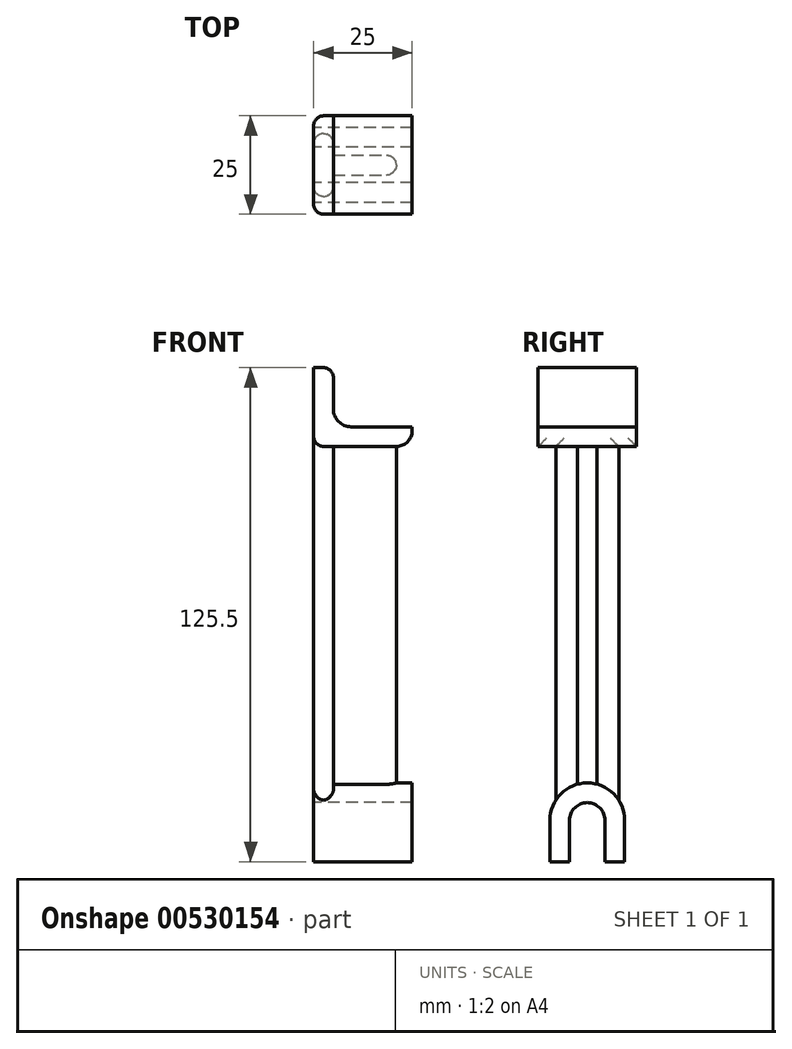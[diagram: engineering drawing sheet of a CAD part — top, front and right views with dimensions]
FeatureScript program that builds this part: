
annotation { "Feature Type Name" : "Feature", "Feature Type Description" : "" }
export const myFeature = defineFeature(function(context is Context, id is Id, definition is map)
    precondition{}
    {
        {
            var Q0;
            Q0=qCreatedBy(makeId("Front.planeOp"),FACE);
            var sketch = newSketch(context, id + "F0", { "sketchPlane" : qUnion([Q0])});
            skCircle(sketch, "E0", {"center": v(0, 104.5) * mm, "radius": 4.5 * mm});
            skLineSegment(sketch, "E1", {"start": v(0, 100) * mm, "end": v(15.5, 100) * mm});
            skLineSegment(sketch, "E2", {"start": v(-4.5, 104.5) * mm, "end": v(-4.5, 115) * mm});
            skLineSegment(sketch, "E3", {"start": v(-4.5, 115) * mm, "end": v(-9.5, 115) * mm});
            skLineSegment(sketch, "E4", {"start": v(-9.5, 115) * mm, "end": v(-9.5, 95) * mm});
            skLineSegment(sketch, "E5", {"start": v(-9.5, 95) * mm, "end": v(15.5, 95) * mm});
            skLineSegment(sketch, "E6", {"start": v(15.5, 95) * mm, "end": v(15.5, 100) * mm});
            skSolve(sketch);
        }
        {
            var Q0;
            {var subQ1=sQuery(id+"F0.wireOp",EDGE,"E1");Q0=makeQuery(id+"F0.imprint","IMPRINT",FACE,{"disambiguationData":[TD([[makeQuery(id+"F0.imprint","IMPRINT",EDGE,{"derivedFrom":subQ1}),-1.0]])]});}
            extrude(context, id + "F1", {"entities" : qUnion([Q0]), "depth" : 25 * mm, "offsetDistance" : 25 * mm, "symmetric" : true});
        }
        {
            var Q0;
            Q0=makeQuery(id+"F1.opExtrude","SWEPT_FACE",FACE,{"disambiguationData":[OSD([sQuery(id+"F0.wireOp",EDGE,"E4")])]});
            var sketch = newSketch(context, id + "F2", { "sketchPlane" : qUnion([Q0])});
            skCircle(sketch, "E7", {"center": v(0, 0) * mm, "radius": 4.5 * mm});
            skLineSegment(sketch, "E8", {"start": v(4.5, 0) * mm, "end": v(4.5, -10.5) * mm});
            skLineSegment(sketch, "E9", {"start": v(4.5, -10.5) * mm, "end": v(9.5, -10.5) * mm});
            skLineSegment(sketch, "E10", {"start": v(9.5, -10.5) * mm, "end": v(9.5, 9.5) * mm});
            skLineSegment(sketch, "E11", {"start": v(9.5, 9.5) * mm, "end": v(-9.5, 9.5) * mm});
            skLineSegment(sketch, "E12", {"start": v(-9.5, 9.5) * mm, "end": v(-9.5, -10.5) * mm});
            skLineSegment(sketch, "E13", {"start": v(-9.5, -10.5) * mm, "end": v(-4.5, -10.5) * mm});
            skLineSegment(sketch, "E14", {"start": v(-4.5, -10.5) * mm, "end": v(-4.5, 0) * mm});
            skArc(sketch, "E15", {"start": v(9.5, 0) * mm, "mid": v(0, 9.5) * mm, "end": v(-9.5, 0) * mm});
            skSolve(sketch);
        }
        {
            var Q0;
            {var subQ4=sQuery(id+"F2.wireOp",EDGE,"E8");Q0=makeQuery(id+"F2.imprint","IMPRINT",FACE,{"disambiguationData":[TD([[makeQuery(id+"F2.imprint","IMPRINT",EDGE,{"derivedFrom":subQ4}),1.0]])]});}
            extrude(context, id + "F3", {"entities" : qUnion([Q0]), "oppositeDirection" : true, "depth" : 25 * mm, "offsetDistance" : 25 * mm});
        }
        {
            var Q0;
            Q0=makeQuery(id+"F1.opExtrude","SWEPT_FACE",FACE,{"disambiguationData":[OSD([sQuery(id+"F0.wireOp",EDGE,"E5")])]});
            var sketch = newSketch(context, id + "F4", { "sketchPlane" : qUnion([Q0])});
            skLineSegment(sketch, "E16.bottom", {"start": v(-9.5, 8) * mm, "end": v(-4.5, 8) * mm});
            skLineSegment(sketch, "E16.top", {"start": v(-9.5, -8) * mm, "end": v(-4.5, -8) * mm});
            skLineSegment(sketch, "E16.left", {"start": v(-9.5, 8) * mm, "end": v(-9.5, -8) * mm});
            skLineSegment(sketch, "E16.right", {"start": v(-4.5, 8) * mm, "end": v(-4.5, -8) * mm});
            skLineSegment(sketch, "E17.bottom", {"start": v(-4.5, 2.5) * mm, "end": v(11.5, 2.5) * mm});
            skLineSegment(sketch, "E17.top", {"start": v(-4.5, -2.5) * mm, "end": v(11.5, -2.5) * mm});
            skLineSegment(sketch, "E17.left", {"start": v(-4.5, 2.5) * mm, "end": v(-4.5, -2.5) * mm});
            skLineSegment(sketch, "E17.right", {"start": v(11.5, 2.5) * mm, "end": v(11.5, -2.5) * mm});
            skSolve(sketch);
        }
        {
            var Q0;
            {var subQ1=sQuery(id+"F4.wireOp",EDGE,"E16.bottom");Q0=makeQuery(id+"F4.imprint","IMPRINT",FACE,{"disambiguationData":[TD([[makeQuery(id+"F4.imprint","IMPRINT",EDGE,{"derivedFrom":subQ1}),-1.0]])]});}
            var Q1;
            Q1=makeQuery(id+"F4.imprint","IMPRINT",FACE,{"disambiguationData":[TD([[makeQuery(id+"F4.imprint","IMPRINT",EDGE,{"derivedFrom":sQuery(id+"F4.wireOp",EDGE,"E17.bottom")}),-1.0]])]});
            extrude(context, id + "F5", {"entities" : qUnion([Q0, Q1]), "operationType" : NewBodyOperationType.ADD, "endBound" : BoundingType.UP_TO_NEXT, "depth" : 25 * mm, "offsetDistance" : 25 * mm});
        }
        {
            var Q0;
            Q0=makeQuery(id+"F1.opExtrude","SWEPT_EDGE",EDGE,{"disambiguationData":[OSD([sQuery(id+"F0.wireOp",EDGE,"E5"),sQuery(id+"F0.wireOp",EDGE,"E6")])]});
            fillet(context, id + "F6", {"entities" : qUnion([Q0]), "radius" : 4 * mm, "tangentPropagation" : true, "allowEdgeOverflow" : false});
        }
        {
            var Q0;
            Q0=makeQuery(id+"F5.opExtrude","SWEPT_EDGE",EDGE,{"disambiguationData":[OSD([sQuery(id+"F4.wireOp",EDGE,"E17.bottom"),sQuery(id+"F4.wireOp",EDGE,"E17.right")])]});
            var Q1;
            Q1=makeQuery(id+"F5.opExtrude","SWEPT_EDGE",EDGE,{"disambiguationData":[OSD([sQuery(id+"F4.wireOp",EDGE,"E17.top"),sQuery(id+"F4.wireOp",EDGE,"E17.right")])]});
            var Q2;
            Q2=makeQuery(id+"F5.opExtrude","SWEPT_EDGE",EDGE,{"disambiguationData":[OSD([sQuery(id+"F4.wireOp",EDGE,"E16.bottom"),sQuery(id+"F4.wireOp",EDGE,"E16.right")])]});
            var Q3;
            Q3=makeQuery(id+"F5.opExtrude","SWEPT_EDGE",EDGE,{"disambiguationData":[OSD([sQuery(id+"F4.wireOp",EDGE,"E16.top"),sQuery(id+"F4.wireOp",EDGE,"E16.right")])]});
            var Q4;
            Q4=makeQuery(id+"F5.opExtrude","SWEPT_EDGE",EDGE,{"disambiguationData":[OSD([sQuery(id+"F0.wireOp",EDGE,"E4"),sQuery(id+"F0.wireOp",EDGE,"E5"),sQuery(id+"F4.wireOp",EDGE,"E16.top"),sQuery(id+"F4.wireOp",EDGE,"E16.left")])]});
            var Q5;
            Q5=makeQuery(id+"F5.opExtrude","SWEPT_EDGE",EDGE,{"disambiguationData":[OSD([sQuery(id+"F0.wireOp",EDGE,"E4"),sQuery(id+"F0.wireOp",EDGE,"E5"),sQuery(id+"F4.wireOp",EDGE,"E16.bottom"),sQuery(id+"F4.wireOp",EDGE,"E16.left")])]});
            var Q6;
            {var subQ0=sQuery(id+"F0.wireOp",EDGE,"E4");var subQ1=sQuery(id+"F0.wireOp",EDGE,"E5");Q6=makeQuery(id+"F5.boolean.opBoolean","SPLIT",EDGE,{"disambiguationData":[TD([makeQuery(id+"F5.opExtrude","SWEPT_FACE",FACE,{"disambiguationData":[OSD([sQuery(id+"F4.wireOp",EDGE,"E16.bottom")])]})])],"derivedFrom":makeQuery(id+"F1.opExtrude","SWEPT_EDGE",EDGE,{"disambiguationData":[OSD([subQ0,subQ1])]})});}
            var Q7;
            {var subQ0=sQuery(id+"F0.wireOp",EDGE,"E5");var subQ1=sQuery(id+"F0.wireOp",EDGE,"E4");Q7=makeQuery(id+"F5.boolean.opBoolean","SPLIT",EDGE,{"disambiguationData":[TD([makeQuery(id+"F5.opExtrude","SWEPT_FACE",FACE,{"disambiguationData":[OSD([sQuery(id+"F4.wireOp",EDGE,"E16.top")])]})])],"derivedFrom":makeQuery(id+"F1.opExtrude","SWEPT_EDGE",EDGE,{"disambiguationData":[OSD([subQ1,subQ0])]})});}
            var Q8;
            Q8=makeQuery(id+"F1.opExtrude","CAP_EDGE",EDGE,{"disambiguationData":[OSD([sQuery(id+"F0.wireOp",EDGE,"E4")])],"isStart":false});
            var Q9;
            Q9=makeQuery(id+"F1.opExtrude","CAP_EDGE",EDGE,{"disambiguationData":[OSD([sQuery(id+"F0.wireOp",EDGE,"E4")])],"isStart":true});
            var Q10;
            Q10=makeQuery(id+"F1.opExtrude","SWEPT_EDGE",EDGE,{"disambiguationData":[OSD([sQuery(id+"F0.wireOp",EDGE,"E2"),sQuery(id+"F0.wireOp",EDGE,"E3")])]});
            fillet(context, id + "F7", {"entities" : qUnion([Q0, Q1, Q2, Q3, Q4, Q5, Q6, Q7, Q8, Q9, Q10]), "radius" : 2.5 * mm, "tangentPropagation" : true, "allowEdgeOverflow" : false});
        }
    });
